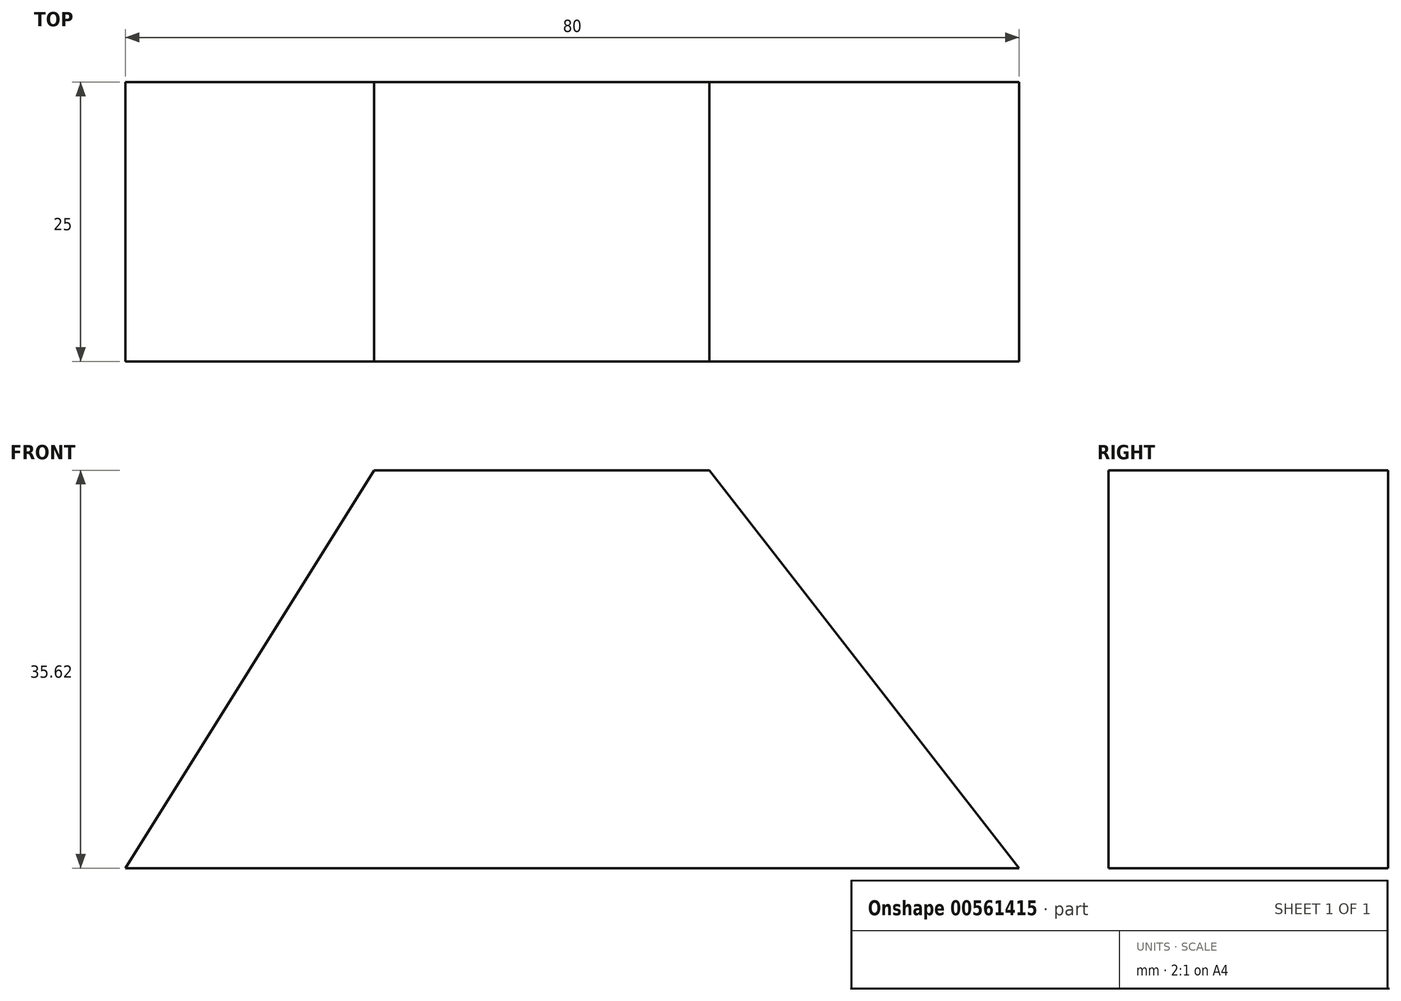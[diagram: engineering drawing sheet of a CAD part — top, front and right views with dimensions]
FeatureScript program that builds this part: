
annotation { "Feature Type Name" : "Feature", "Feature Type Description" : "" }
export const myFeature = defineFeature(function(context is Context, id is Id, definition is map)
    precondition{}
    {
        {
            var Q0;
            Q0=qCreatedBy(makeId("Front.planeOp"),FACE);
            var sketch = newSketch(context, id + "F0", { "sketchPlane" : qUnion([Q0])});
            skLineSegment(sketch, "E0", {"start": v(-18.7, -22.47) * mm, "end": v(61.3, -22.47) * mm});
            skLineSegment(sketch, "E1", {"start": v(61.3, -22.47) * mm, "end": v(33.56, 13.15) * mm});
            skLineSegment(sketch, "E2", {"start": v(33.56, 13.15) * mm, "end": v(3.56, 13.15) * mm});
            skLineSegment(sketch, "E3", {"start": v(3.56, 13.15) * mm, "end": v(-18.7, -22.47) * mm});
            skSolve(sketch);
        }
        {
            var Q0;
            Q0 = qSketchRegion(id + "F0", true);
            extrude(context, id + "F1", {"entities" : qUnion([Q0]), "depth" : 25 * mm, "offsetDistance" : 25 * mm});
        }
    });
